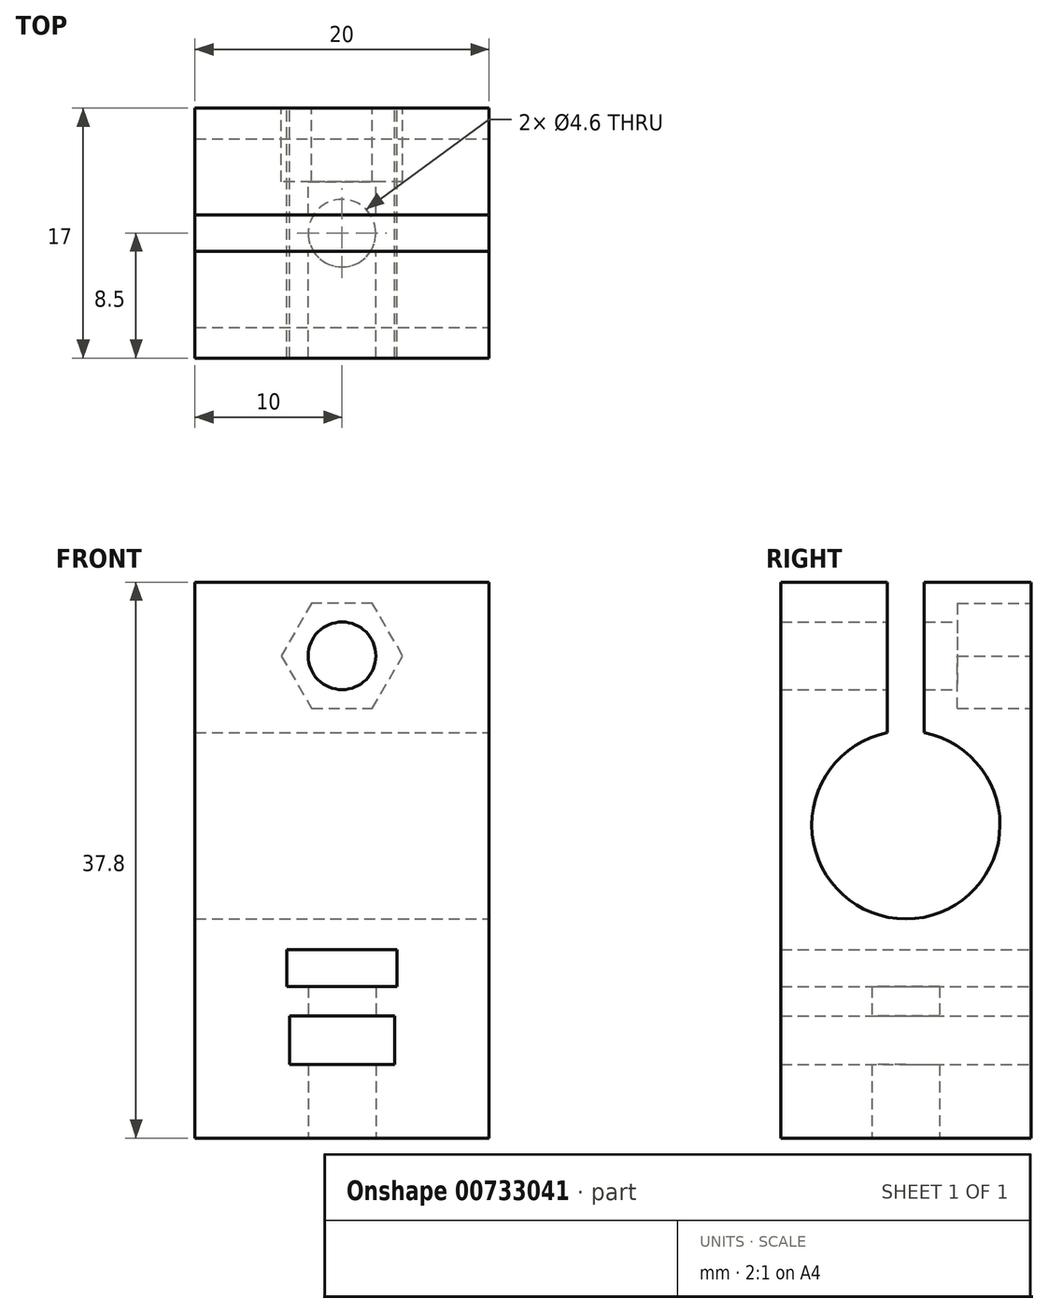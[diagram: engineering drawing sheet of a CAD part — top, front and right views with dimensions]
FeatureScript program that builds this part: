
annotation { "Feature Type Name" : "Feature", "Feature Type Description" : "" }
export const myFeature = defineFeature(function(context is Context, id is Id, definition is map)
    precondition{}
    {
        {
            var Q0;
            Q0=qCreatedBy(makeId("Front.planeOp"),FACE);
            var sketch = newSketch(context, id + "F0", { "sketchPlane" : qUnion([Q0])});
            skLineSegment(sketch, "E0.bottom", {"start": v(-10, 0) * mm, "end": v(10, 0) * mm});
            skLineSegment(sketch, "E0.top", {"start": v(-10, 37.8) * mm, "end": v(10, 37.8) * mm});
            skLineSegment(sketch, "E0.left", {"start": v(-10, 0) * mm, "end": v(-10, 37.8) * mm});
            skLineSegment(sketch, "E0.right", {"start": v(10, 0) * mm, "end": v(10, 37.8) * mm});
            skLineSegment(sketch, "E1.bottom", {"start": v(-3.58, 8.3) * mm, "end": v(3.58, 8.3) * mm});
            skLineSegment(sketch, "E1.top", {"start": v(-3.57, 5) * mm, "end": v(3.57, 5) * mm});
            skLineSegment(sketch, "E1.left", {"start": v(-3.57, 8.3) * mm, "end": v(-3.58, 5) * mm});
            skLineSegment(sketch, "E1.right", {"start": v(3.58, 8.3) * mm, "end": v(3.58, 5) * mm});
            skLineSegment(sketch, "E2.bottom", {"start": v(-3.75, 12.8) * mm, "end": v(3.75, 12.8) * mm});
            skLineSegment(sketch, "E2.top", {"start": v(-3.75, 10.3) * mm, "end": v(3.75, 10.3) * mm});
            skLineSegment(sketch, "E2.left", {"start": v(-3.75, 12.8) * mm, "end": v(-3.75, 10.3) * mm});
            skLineSegment(sketch, "E2.right", {"start": v(3.75, 12.8) * mm, "end": v(3.75, 10.3) * mm});
            skSolve(sketch);
        }
        {
            var Q0;
            Q0 = qSketchRegion(id + "F0", true);
            extrude(context, id + "F1", {"entities" : qUnion([Q0]), "depth" : 17 * mm, "offsetDistance" : 25 * mm});
        }
        {
            var Q0;
            Q0=makeQuery(id+"F1.opExtrude","SWEPT_FACE",FACE,{"disambiguationData":[OSD([sQuery(id+"F0.wireOp",EDGE,"E0.right")])]});
            var sketch = newSketch(context, id + "F2", { "sketchPlane" : qUnion([Q0])});
            skLineSegment(sketch, "E3", {"start": v(-8.5, 42.88) * mm, "end": v(-8.5, -6.83) * mm, "construction": true});
            skPoint(sketch, "E3.startSnap0", {"position": v(-8.5, 37.8) * mm});
            skPoint(sketch, "E3.endSnap0", {"position": v(-8.5, 0) * mm});
            skLineSegment(sketch, "E4", {"start": v(-23.08, 21.3) * mm, "end": v(8.17, 21.3) * mm, "construction": true});
            skArc(sketch, "E5", {"start": v(-9.75, 27.58) * mm, "mid": v(-8.5, 14.9) * mm, "end": v(-7.25, 27.58) * mm});
            skLineSegment(sketch, "E6.bottom", {"start": v(-9.75, 39.09) * mm, "end": v(-7.25, 39.09) * mm});
            skLineSegment(sketch, "E6.left", {"start": v(-9.75, 39.09) * mm, "end": v(-9.75, 27.58) * mm});
            skLineSegment(sketch, "E6.right", {"start": v(-7.25, 39.09) * mm, "end": v(-7.25, 27.58) * mm});
            skPoint(sketch, "E7.orphan", {"position": v(-9.75, 25.91) * mm});
            skPoint(sketch, "E8.orphan", {"position": v(-7.25, 25.91) * mm});
            skSolve(sketch);
        }
        {
            var Q0;
            Q0 = qSketchRegion(id + "F2", true);
            extrude(context, id + "F3", {"entities" : qUnion([Q0]), "operationType" : NewBodyOperationType.REMOVE, "endBound" : BoundingType.THROUGH_ALL, "oppositeDirection" : true, "depth" : 25 * mm, "offsetDistance" : 25 * mm});
        }
        {
            var Q0;
            Q0=makeQuery(id+"F1.opExtrude","CAP_FACE",FACE,{"disambiguationData":[OSD([sQuery(id+"F0.wireOp",EDGE,"E0.bottom"),sQuery(id+"F0.wireOp",EDGE,"E0.top"),sQuery(id+"F0.wireOp",EDGE,"E0.left"),sQuery(id+"F0.wireOp",EDGE,"E0.right"),sQuery(id+"F0.wireOp",EDGE,"E1.bottom"),sQuery(id+"F0.wireOp",EDGE,"E1.top"),sQuery(id+"F0.wireOp",EDGE,"E1.left"),sQuery(id+"F0.wireOp",EDGE,"E1.right"),sQuery(id+"F0.wireOp",EDGE,"E2.bottom"),sQuery(id+"F0.wireOp",EDGE,"E2.top"),sQuery(id+"F0.wireOp",EDGE,"E2.left"),sQuery(id+"F0.wireOp",EDGE,"E2.right")])],"isStart":true});
            var sketch = newSketch(context, id + "F4", { "sketchPlane" : qUnion([Q0])});
            skCircle(sketch, "E9", {"center": v(0, 32.8) * mm, "radius": 2.3 * mm});
            skSolve(sketch);
        }
        {
            var Q0;
            Q0 = qSketchRegion(id + "F4", true);
            extrude(context, id + "F5", {"entities" : qUnion([Q0]), "operationType" : NewBodyOperationType.REMOVE, "endBound" : BoundingType.THROUGH_ALL, "oppositeDirection" : true, "depth" : 25 * mm, "offsetDistance" : 25 * mm});
        }
        {
            var Q0;
            Q0=makeQuery(id+"F1.opExtrude","CAP_FACE",FACE,{"disambiguationData":[OSD([sQuery(id+"F0.wireOp",EDGE,"E0.bottom"),sQuery(id+"F0.wireOp",EDGE,"E0.top"),sQuery(id+"F0.wireOp",EDGE,"E0.left"),sQuery(id+"F0.wireOp",EDGE,"E0.right"),sQuery(id+"F0.wireOp",EDGE,"E1.bottom"),sQuery(id+"F0.wireOp",EDGE,"E1.top"),sQuery(id+"F0.wireOp",EDGE,"E1.left"),sQuery(id+"F0.wireOp",EDGE,"E1.right"),sQuery(id+"F0.wireOp",EDGE,"E2.bottom"),sQuery(id+"F0.wireOp",EDGE,"E2.top"),sQuery(id+"F0.wireOp",EDGE,"E2.left"),sQuery(id+"F0.wireOp",EDGE,"E2.right")])],"isStart":true});
            var sketch = newSketch(context, id + "F6", { "sketchPlane" : qUnion([Q0])});
            skCircle(sketch, "E10.cCircle", {"center": v(0, 32.8) * mm, "radius": 3.57 * mm, "construction": true});
            skLineSegment(sketch, "E10.0", {"start": v(2.06, 36.38) * mm, "end": v(4.13, 32.8) * mm});
            skLineSegment(sketch, "E10.1", {"start": v(4.13, 32.8) * mm, "end": v(2.06, 29.23) * mm});
            skLineSegment(sketch, "E10.2", {"start": v(2.06, 29.23) * mm, "end": v(-2.06, 29.23) * mm});
            skLineSegment(sketch, "E10.3", {"start": v(-2.06, 29.23) * mm, "end": v(-4.13, 32.8) * mm});
            skLineSegment(sketch, "E10.4", {"start": v(-4.13, 32.8) * mm, "end": v(-2.06, 36.38) * mm});
            skLineSegment(sketch, "E10.5", {"start": v(-2.06, 36.38) * mm, "end": v(2.06, 36.38) * mm});
            skPoint(sketch, "E10.0.midPoint", {"position": v(3.1, 34.59) * mm});
            skSolve(sketch);
        }
        {
            var Q0;
            Q0 = qSketchRegion(id + "F6", true);
            extrude(context, id + "F7", {"entities" : qUnion([Q0]), "operationType" : NewBodyOperationType.REMOVE, "oppositeDirection" : true, "depth" : 5 * mm, "offsetDistance" : 25 * mm});
        }
        {
            var Q0;
            Q0=makeQuery(id+"F1.opExtrude","SWEPT_FACE",FACE,{"disambiguationData":[OSD([sQuery(id+"F0.wireOp",EDGE,"E0.bottom")])]});
            var sketch = newSketch(context, id + "F8", { "sketchPlane" : qUnion([Q0])});
            skCircle(sketch, "E11", {"center": v(0, 8.5) * mm, "radius": 2.3 * mm});
            skPoint(sketch, "E11.centerSnap0", {"position": v(10, 8.5) * mm});
            skSolve(sketch);
        }
        {
            var Q0;
            Q0 = qSketchRegion(id + "F8", true);
            extrude(context, id + "F9", {"entities" : qUnion([Q0]), "operationType" : NewBodyOperationType.REMOVE, "oppositeDirection" : true, "depth" : 11 * mm, "offsetDistance" : 25 * mm});
        }
    });
